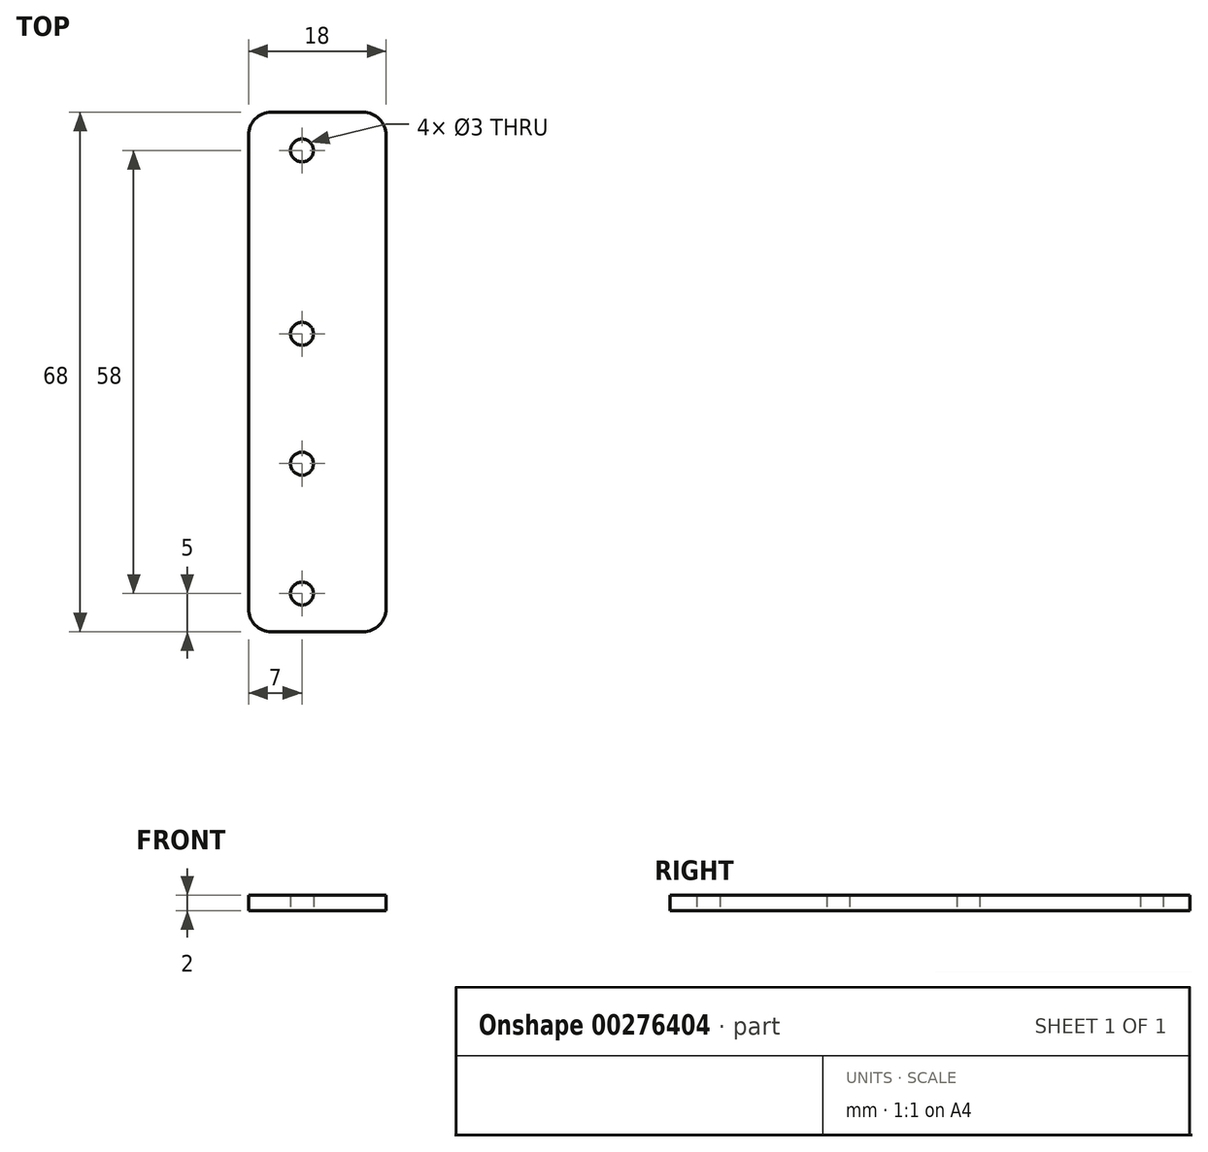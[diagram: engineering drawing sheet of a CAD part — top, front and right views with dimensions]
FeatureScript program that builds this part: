
annotation { "Feature Type Name" : "Feature", "Feature Type Description" : "" }
export const myFeature = defineFeature(function(context is Context, id is Id, definition is map)
    precondition{}
    {
        {
            var Q0;
            Q0=qCreatedBy(makeId("Top.planeOp"),FACE);
            var sketch = newSketch(context, id + "F0", { "sketchPlane" : qUnion([Q0])});
            skLineSegment(sketch, "E0.bottom", {"start": v(0, 0) * mm, "end": v(18, 0) * mm});
            skLineSegment(sketch, "E0.top", {"start": v(0, 68) * mm, "end": v(18, 68) * mm});
            skLineSegment(sketch, "E0.right", {"start": v(18, 0) * mm, "end": v(18, 68) * mm});
            skCircle(sketch, "E1", {"center": v(7, 5) * mm, "radius": 1.5 * mm});
            skCircle(sketch, "E2", {"center": v(7, 22) * mm, "radius": 1.5 * mm});
            skCircle(sketch, "E3", {"center": v(7, 39) * mm, "radius": 1.5 * mm});
            skLineSegment(sketch, "E4", {"start": v(0, 68) * mm, "end": v(0, 0) * mm});
            skCircle(sketch, "E5", {"center": v(7, 63) * mm, "radius": 1.5 * mm});
            skSolve(sketch);
        }
        {
            var Q0;
            Q0=qSketchRegion(id+"F0",true);
            extrude(context, id + "F1", {"entities" : qUnion([Q0]), "depth" : 2 * mm});
        }
        {
            var Q0;
            Q0=makeQuery(id+"F1.opExtrude","SWEPT_EDGE",EDGE,{"disambiguationData":[OSD([sQuery(id+"F0.wireOp",EDGE,"E0.top"),sQuery(id+"F0.wireOp",EDGE,"E0.right")])]});
            var Q1;
            Q1=makeQuery(id+"F1.opExtrude","SWEPT_EDGE",EDGE,{"disambiguationData":[OSD([sQuery(id+"F0.wireOp",EDGE,"E0.top"),sQuery(id+"F0.wireOp",EDGE,"E4")])]});
            var Q2;
            Q2=makeQuery(id+"F1.opExtrude","SWEPT_EDGE",EDGE,{"disambiguationData":[OSD([sQuery(id+"F0.wireOp",EDGE,"E0.bottom"),sQuery(id+"F0.wireOp",EDGE,"E0.right")])]});
            var Q3;
            Q3=makeQuery(id+"F1.opExtrude","SWEPT_EDGE",EDGE,{"disambiguationData":[OSD([sQuery(id+"F0.wireOp",EDGE,"E0.bottom"),sQuery(id+"F0.wireOp",EDGE,"E4")])]});
            fillet(context, id + "F2", {"entities" : qUnion([Q0, Q1, Q2, Q3]), "tangentPropagation" : true, "radius" : 3 * mm, "defaultsChanged" : false, "vertexSettings" : [], "allowEdgeOverflow" : false});
        }
    });
